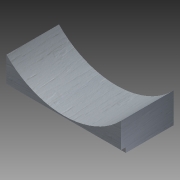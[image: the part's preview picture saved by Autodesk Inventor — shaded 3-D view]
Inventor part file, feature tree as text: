
AUTODESK INVENTOR PART (.ipt)
format: ipt  version: 2011 SP1 (Build 150282100, 282)  size: 93,696 bytes
history: native  units: in
note: dims shown in document units (in); Inventor stores cm internally (conversion verified against a paired STEP export)
features: other x3, extrude x1, sketch x1
ambient origin geometry x8: Origin, YZ Plane, XZ Plane, XY Plane, X Axis, Y Axis, Z Axis, Center Point
bodies: Solid1 (feature_tree)
feature tree (5):
  other  "Duct_Support.ipt"
  extrude  "Extrusion1"  Depth=0.25in
  other  "Solid1::Duct_Support.ipt"
  other  "TaggingFeature1"
  sketch  "Sketch2"  dims[d0=0.3937in d1=0.25in d2=0.25in d3=6.0in d4=0.0in]
